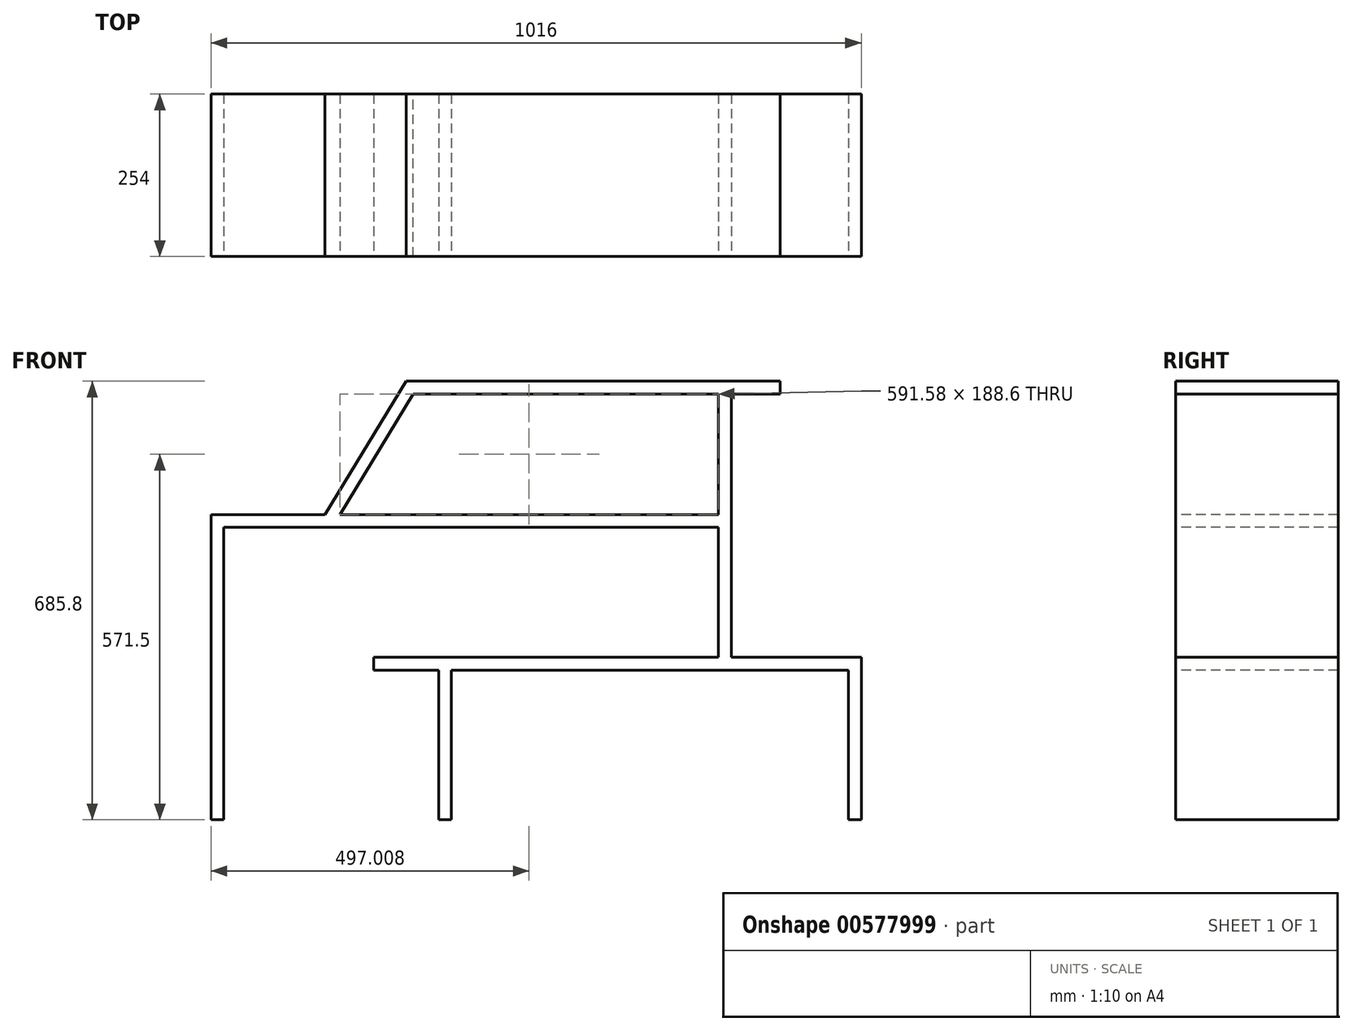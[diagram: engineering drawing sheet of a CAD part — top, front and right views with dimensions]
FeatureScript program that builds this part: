
annotation { "Feature Type Name" : "Feature", "Feature Type Description" : "" }
export const myFeature = defineFeature(function(context is Context, id is Id, definition is map)
    precondition{}
    {
        {
            var Q0;
            Q0=qCreatedBy(makeId("Top.planeOp"),FACE);
            var sketch = newSketch(context, id + "F0", { "sketchPlane" : qUnion([Q0])});
            skLineSegment(sketch, "E0", {"start": v(-526.18, 0) * mm, "end": v(427.5, 0) * mm, "construction": true});
            skLineSegment(sketch, "E1", {"start": v(0, -163.77) * mm, "end": v(0, 241.83) * mm, "construction": true});
            skLineSegment(sketch, "E2.bottom", {"start": v(488, 127) * mm, "end": v(508, 127) * mm});
            skLineSegment(sketch, "E2.top", {"start": v(488, -127) * mm, "end": v(508, -127) * mm});
            skLineSegment(sketch, "E2.left", {"start": v(488, 127) * mm, "end": v(488, -127) * mm});
            skLineSegment(sketch, "E2.right", {"start": v(508, 127) * mm, "end": v(508, -127) * mm});
            skSolve(sketch);
        }
        {
            var Q0;
            Q0=makeQuery(id+"F0.imprint","IMPRINT",FACE,{"disambiguationData":[TD([[makeQuery(id+"F0.imprint","IMPRINT",EDGE,{"derivedFrom":sQuery(id+"F0.wireOp",EDGE,"E2.bottom")}),-1.0]])]});
            extrude(context, id + "F1", {"entities" : qUnion([Q0]), "depth" : 254 * mm, "offsetDistance" : 25.4 * mm});
        }
        {
            var Q0;
            Q0=makeQuery(id+"F1.opExtrude","SWEPT_FACE",FACE,{"disambiguationData":[OSD([sQuery(id+"F0.wireOp",EDGE,"E2.top")])]});
            var sketch = newSketch(context, id + "F2", { "sketchPlane" : qUnion([Q0])});
            skLineSegment(sketch, "E3.bottom", {"start": v(508, 234) * mm, "end": v(-254, 234) * mm});
            skLineSegment(sketch, "E3.top", {"start": v(508, 254) * mm, "end": v(-254, 254) * mm});
            skLineSegment(sketch, "E3.left", {"start": v(508, 234) * mm, "end": v(508, 254) * mm});
            skLineSegment(sketch, "E3.right", {"start": v(-254, 234) * mm, "end": v(-254, 254) * mm});
            skSolve(sketch);
        }
        {
            var Q0;
            Q0=makeQuery(id+"F2.imprint","IMPRINT",FACE,{"disambiguationData":[TD([[makeQuery(id+"F2.imprint","IMPRINT",EDGE,{"derivedFrom":sQuery(id+"F2.wireOp",EDGE,"E3.top")}),1.0]])]});
            var Q1;
            Q1=makeQuery(id+"F1.opExtrude","SWEPT_FACE",FACE,{"disambiguationData":[OSD([sQuery(id+"F0.wireOp",EDGE,"E2.bottom")])]});
            extrude(context, id + "F3", {"entities" : qUnion([Q0]), "operationType" : NewBodyOperationType.ADD, "endBound" : BoundingType.UP_TO_SURFACE, "oppositeDirection" : true, "depth" : 25.4 * mm, "endBoundEntityFace" : qUnion([Q1]), "offsetDistance" : 25.4 * mm});
        }
        {
            var Q0;
            Q0=makeQuery(id+"F3.boolean.opBoolean","MERGE",FACE,{"derivedFrom":[makeQuery(id+"F1.opExtrude","SWEPT_FACE",FACE,{"disambiguationData":[OSD([sQuery(id+"F0.wireOp",EDGE,"E2.top")])]}),makeQuery(id+"F3.opExtrude","CAP_FACE",FACE,{"disambiguationData":[OSD([sQuery(id+"F2.wireOp",EDGE,"E3.bottom"),sQuery(id+"F2.wireOp",EDGE,"E3.top"),sQuery(id+"F2.wireOp",EDGE,"E3.left"),sQuery(id+"F2.wireOp",EDGE,"E3.right")])],"isStart":true})]});
            var sketch = newSketch(context, id + "F4", { "sketchPlane" : qUnion([Q0])});
            skLineSegment(sketch, "E4.bottom", {"start": v(-152.4, 234) * mm, "end": v(-132.4, 234) * mm});
            skLineSegment(sketch, "E4.top", {"start": v(-152.4, 0) * mm, "end": v(-132.4, 0) * mm});
            skLineSegment(sketch, "E4.left", {"start": v(-152.4, 234) * mm, "end": v(-152.4, 0) * mm});
            skLineSegment(sketch, "E4.right", {"start": v(-132.4, 234) * mm, "end": v(-132.4, 0) * mm});
            skSolve(sketch);
        }
        {
            var Q0;
            Q0=makeQuery(id+"F4.imprint","IMPRINT",FACE,{"disambiguationData":[TD([[makeQuery(id+"F4.imprint","IMPRINT",EDGE,{"derivedFrom":sQuery(id+"F4.wireOp",EDGE,"E4.bottom")}),1.0]])]});
            var Q1;
            {var subQ0=sQuery(id+"F0.wireOp",EDGE,"E2.bottom");Q1=makeQuery(id+"F3.boolean.opBoolean","MERGE",FACE,{"derivedFrom":[makeQuery(id+"F1.opExtrude","SWEPT_FACE",FACE,{"disambiguationData":[OSD([subQ0])]}),makeQuery(id+"F3.opExtrude","CAP_FACE",FACE,{"disambiguationData":[OSD([subQ0])],"isStart":false})]});}
            extrude(context, id + "F5", {"entities" : qUnion([Q0]), "operationType" : NewBodyOperationType.ADD, "endBound" : BoundingType.UP_TO_SURFACE, "oppositeDirection" : true, "depth" : 25.4 * mm, "endBoundEntityFace" : qUnion([Q1]), "offsetDistance" : 25.4 * mm});
        }
        {
            var Q0;
            Q0=makeQuery(id+"F5.boolean.opBoolean","MERGE",FACE,{"derivedFrom":[makeQuery(id+"F3.boolean.opBoolean","MERGE",FACE,{"derivedFrom":[makeQuery(id+"F1.opExtrude","SWEPT_FACE",FACE,{"disambiguationData":[OSD([sQuery(id+"F0.wireOp",EDGE,"E2.top")])]}),makeQuery(id+"F3.opExtrude","CAP_FACE",FACE,{"disambiguationData":[OSD([sQuery(id+"F2.wireOp",EDGE,"E3.bottom"),sQuery(id+"F2.wireOp",EDGE,"E3.top"),sQuery(id+"F2.wireOp",EDGE,"E3.left"),sQuery(id+"F2.wireOp",EDGE,"E3.right")])],"isStart":true})]}),makeQuery(id+"F5.opExtrude","CAP_FACE",FACE,{"disambiguationData":[OSD([sQuery(id+"F4.wireOp",EDGE,"E4.bottom"),sQuery(id+"F4.wireOp",EDGE,"E4.top"),sQuery(id+"F4.wireOp",EDGE,"E4.left"),sQuery(id+"F4.wireOp",EDGE,"E4.right")])],"isStart":true})]});
            var sketch = newSketch(context, id + "F6", { "sketchPlane" : qUnion([Q0])});
            skLineSegment(sketch, "E5.bottom", {"start": v(304.8, 254) * mm, "end": v(284.8, 254) * mm});
            skLineSegment(sketch, "E5.top", {"start": v(304.8, 665.8) * mm, "end": v(284.8, 665.8) * mm});
            skLineSegment(sketch, "E5.left", {"start": v(284.8, 254) * mm, "end": v(284.8, 665.8) * mm});
            skLineSegment(sketch, "E5.right", {"start": v(304.8, 254) * mm, "end": v(304.8, 665.8) * mm});
            skSolve(sketch);
        }
        {
            var Q0;
            Q0=makeQuery(id+"F6.imprint","IMPRINT",FACE,{"disambiguationData":[TD([[makeQuery(id+"F6.imprint","IMPRINT",EDGE,{"derivedFrom":sQuery(id+"F6.wireOp",EDGE,"E5.bottom")}),-1.0]])]});
            var Q1;
            Q1=makeQuery(id+"F6.imprint","IMPRINT",FACE,{"disambiguationData":[TD([[makeQuery(id+"F6.imprint","IMPRINT",EDGE,{"derivedFrom":sQuery(id+"F6.wireOp",EDGE,"E5.bottom")}),1.0]])]});
            var Q2;
            {var subQ0=sQuery(id+"F0.wireOp",EDGE,"E2.bottom");Q2=makeQuery(id+"F5.boolean.opBoolean","MERGE",FACE,{"derivedFrom":[makeQuery(id+"F3.boolean.opBoolean","MERGE",FACE,{"derivedFrom":[makeQuery(id+"F1.opExtrude","SWEPT_FACE",FACE,{"disambiguationData":[OSD([subQ0])]}),makeQuery(id+"F3.opExtrude","CAP_FACE",FACE,{"disambiguationData":[OSD([subQ0])],"isStart":false})]}),makeQuery(id+"F5.opExtrude","CAP_FACE",FACE,{"disambiguationData":[OSD([subQ0])],"isStart":false})]});}
            extrude(context, id + "F7", {"entities" : qUnion([Q0, Q1]), "operationType" : NewBodyOperationType.ADD, "endBound" : BoundingType.UP_TO_SURFACE, "oppositeDirection" : true, "depth" : 25.4 * mm, "endBoundEntityFace" : qUnion([Q2]), "offsetDistance" : 25.4 * mm});
        }
        {
            var Q0;
            Q0=makeQuery(id+"F7.boolean.opBoolean","MERGE",FACE,{"derivedFrom":[makeQuery(id+"F5.boolean.opBoolean","MERGE",FACE,{"derivedFrom":[makeQuery(id+"F3.boolean.opBoolean","MERGE",FACE,{"derivedFrom":[makeQuery(id+"F1.opExtrude","SWEPT_FACE",FACE,{"disambiguationData":[OSD([sQuery(id+"F0.wireOp",EDGE,"E2.top")])]}),makeQuery(id+"F3.opExtrude","CAP_FACE",FACE,{"disambiguationData":[OSD([sQuery(id+"F2.wireOp",EDGE,"E3.bottom"),sQuery(id+"F2.wireOp",EDGE,"E3.top"),sQuery(id+"F2.wireOp",EDGE,"E3.left"),sQuery(id+"F2.wireOp",EDGE,"E3.right")])],"isStart":true})]}),makeQuery(id+"F5.opExtrude","CAP_FACE",FACE,{"disambiguationData":[OSD([sQuery(id+"F4.wireOp",EDGE,"E4.bottom"),sQuery(id+"F4.wireOp",EDGE,"E4.top"),sQuery(id+"F4.wireOp",EDGE,"E4.left"),sQuery(id+"F4.wireOp",EDGE,"E4.right")])],"isStart":true})]}),makeQuery(id+"F7.opExtrude","CAP_FACE",FACE,{"disambiguationData":[OSD([sQuery(id+"F6.wireOp",EDGE,"E5.bottom"),sQuery(id+"F6.wireOp",EDGE,"E5.top"),sQuery(id+"F6.wireOp",EDGE,"E5.left"),sQuery(id+"F6.wireOp",EDGE,"E5.right")])],"isStart":true})]});
            var sketch = newSketch(context, id + "F8", { "sketchPlane" : qUnion([Q0])});
            skLineSegment(sketch, "E6.bottom", {"start": v(284.8, 477.2) * mm, "end": v(-508, 477.2) * mm});
            skLineSegment(sketch, "E6.top", {"start": v(284.8, 457.2) * mm, "end": v(-508, 457.2) * mm});
            skLineSegment(sketch, "E6.left", {"start": v(284.8, 477.2) * mm, "end": v(284.8, 457.2) * mm});
            skLineSegment(sketch, "E6.right", {"start": v(-508, 477.2) * mm, "end": v(-508, 457.2) * mm});
            skSolve(sketch);
        }
        {
            var Q0;
            Q0=makeQuery(id+"F8.imprint","IMPRINT",FACE,{"disambiguationData":[TD([[makeQuery(id+"F8.imprint","IMPRINT",EDGE,{"derivedFrom":sQuery(id+"F8.wireOp",EDGE,"E6.bottom")}),1.0]])]});
            var Q1;
            {var subQ0=sQuery(id+"F0.wireOp",EDGE,"E2.bottom");Q1=makeQuery(id+"F7.boolean.opBoolean","MERGE",FACE,{"derivedFrom":[makeQuery(id+"F5.boolean.opBoolean","MERGE",FACE,{"derivedFrom":[makeQuery(id+"F3.boolean.opBoolean","MERGE",FACE,{"derivedFrom":[makeQuery(id+"F1.opExtrude","SWEPT_FACE",FACE,{"disambiguationData":[OSD([subQ0])]}),makeQuery(id+"F3.opExtrude","CAP_FACE",FACE,{"disambiguationData":[OSD([subQ0])],"isStart":false})]}),makeQuery(id+"F5.opExtrude","CAP_FACE",FACE,{"disambiguationData":[OSD([subQ0])],"isStart":false})]}),makeQuery(id+"F7.opExtrude","CAP_FACE",FACE,{"disambiguationData":[OSD([subQ0])],"isStart":false})]});}
            extrude(context, id + "F9", {"entities" : qUnion([Q0]), "operationType" : NewBodyOperationType.ADD, "endBound" : BoundingType.UP_TO_SURFACE, "oppositeDirection" : true, "depth" : 25.4 * mm, "endBoundEntityFace" : qUnion([Q1]), "offsetDistance" : 25.4 * mm});
        }
        {
            var Q0;
            Q0=makeQuery(id+"FAE3QQXWs17RaLg_1.boolean.opBoolean","MERGE",FACE,{"derivedFrom":[makeQuery(id+"F7.boolean.opBoolean","MERGE",FACE,{"derivedFrom":[makeQuery(id+"F5.boolean.opBoolean","MERGE",FACE,{"derivedFrom":[makeQuery(id+"F3.boolean.opBoolean","MERGE",FACE,{"derivedFrom":[makeQuery(id+"F1.opExtrude","SWEPT_FACE",FACE,{"disambiguationData":[OSD([sQuery(id+"F0.wireOp",EDGE,"E2.top")])]}),makeQuery(id+"F3.opExtrude","CAP_FACE",FACE,{"disambiguationData":[OSD([sQuery(id+"F2.wireOp",EDGE,"E3.bottom"),sQuery(id+"F2.wireOp",EDGE,"E3.top"),sQuery(id+"F2.wireOp",EDGE,"E3.left"),sQuery(id+"F2.wireOp",EDGE,"E3.right")])],"isStart":true})]}),makeQuery(id+"F5.opExtrude","CAP_FACE",FACE,{"disambiguationData":[OSD([sQuery(id+"F4.wireOp",EDGE,"E4.bottom"),sQuery(id+"F4.wireOp",EDGE,"E4.top"),sQuery(id+"F4.wireOp",EDGE,"E4.left"),sQuery(id+"F4.wireOp",EDGE,"E4.right")])],"isStart":true})]}),makeQuery(id+"F7.opExtrude","CAP_FACE",FACE,{"disambiguationData":[OSD([sQuery(id+"F6.wireOp",EDGE,"E5.bottom"),sQuery(id+"F6.wireOp",EDGE,"E5.top"),sQuery(id+"F6.wireOp",EDGE,"E5.left"),sQuery(id+"F6.wireOp",EDGE,"E5.right")])],"isStart":true})]}),makeQuery(id+"FAE3QQXWs17RaLg_1.opExtrude","CAP_FACE",FACE,{"disambiguationData":[OSD([sQuery(id+"F8.wireOp",EDGE,"uR3yEGrp-6eCu-huob-Tspo-hjttsWu1FWy0.bottom"),sQuery(id+"F8.wireOp",EDGE,"uR3yEGrp-6eCu-huob-Tspo-hjttsWu1FWy0.top"),sQuery(id+"F8.wireOp",EDGE,"uR3yEGrp-6eCu-huob-Tspo-hjttsWu1FWy0.left"),sQuery(id+"F8.wireOp",EDGE,"uR3yEGrp-6eCu-huob-Tspo-hjttsWu1FWy0.right")])],"isStart":true})]});
            var sketch = newSketch(context, id + "F10", { "sketchPlane" : qUnion([Q0])});
            skSolve(sketch);
        }
        {
            var Q0;
            {var subQ6=sQuery(id+"F0.wireOp",EDGE,"E2.top");Q0=makeQuery(id+"F10.imprint","IMPRINT",FACE,{"disambiguationData":[TD([[makeQuery(id+"F10.imprint","IMPRINT",EDGE,{"derivedFrom":makeQuery(id+"F1.opExtrude","CAP_EDGE",EDGE,{"disambiguationData":[OSD([subQ6])],"isStart":true})}),1.0]])]});}
            var sketch = newSketch(context, id + "F11", { "sketchPlane" : qUnion([Q0])});
            skLineSegment(sketch, "E7.bottom", {"start": v(-488, 0) * mm, "end": v(-508, 0) * mm});
            skLineSegment(sketch, "E7.top", {"start": v(-488, 457.2) * mm, "end": v(-508, 457.2) * mm});
            skLineSegment(sketch, "E7.left", {"start": v(-488, 0) * mm, "end": v(-488, 457.2) * mm});
            skLineSegment(sketch, "E7.right", {"start": v(-508, 0) * mm, "end": v(-508, 457.2) * mm});
            skSolve(sketch);
        }
        {
            var Q0;
            Q0=makeQuery(id+"F11.imprint","IMPRINT",FACE,{"disambiguationData":[TD([[makeQuery(id+"F11.imprint","IMPRINT",EDGE,{"derivedFrom":sQuery(id+"F11.wireOp",EDGE,"E7.bottom")}),-1.0]])]});
            var Q1;
            {var subQ0=sQuery(id+"F0.wireOp",EDGE,"E2.bottom");Q1=makeQuery(id+"FAE3QQXWs17RaLg_1.boolean.opBoolean","MERGE",FACE,{"derivedFrom":[makeQuery(id+"F7.boolean.opBoolean","MERGE",FACE,{"derivedFrom":[makeQuery(id+"F5.boolean.opBoolean","MERGE",FACE,{"derivedFrom":[makeQuery(id+"F3.boolean.opBoolean","MERGE",FACE,{"derivedFrom":[makeQuery(id+"F1.opExtrude","SWEPT_FACE",FACE,{"disambiguationData":[OSD([subQ0])]}),makeQuery(id+"F3.opExtrude","CAP_FACE",FACE,{"disambiguationData":[OSD([subQ0])],"isStart":false})]}),makeQuery(id+"F5.opExtrude","CAP_FACE",FACE,{"disambiguationData":[OSD([subQ0])],"isStart":false})]}),makeQuery(id+"F7.opExtrude","CAP_FACE",FACE,{"disambiguationData":[OSD([subQ0])],"isStart":false})]}),makeQuery(id+"FAE3QQXWs17RaLg_1.opExtrude","CAP_FACE",FACE,{"disambiguationData":[OSD([subQ0])],"isStart":false})]});}
            extrude(context, id + "F12", {"entities" : qUnion([Q0]), "operationType" : NewBodyOperationType.ADD, "endBound" : BoundingType.UP_TO_SURFACE, "oppositeDirection" : true, "depth" : 25.4 * mm, "endBoundEntityFace" : qUnion([Q1]), "offsetDistance" : 25.4 * mm});
        }
        {
            var Q0;
            Q0=makeQuery(id+"FF1zM3mXEk5meAQ_1.boolean.opBoolean","MERGE",FACE,{"derivedFrom":[makeQuery(id+"F9.boolean.opBoolean","MERGE",FACE,{"derivedFrom":[makeQuery(id+"F7.boolean.opBoolean","MERGE",FACE,{"derivedFrom":[makeQuery(id+"F5.boolean.opBoolean","MERGE",FACE,{"derivedFrom":[makeQuery(id+"F3.boolean.opBoolean","MERGE",FACE,{"derivedFrom":[makeQuery(id+"F1.opExtrude","SWEPT_FACE",FACE,{"disambiguationData":[OSD([sQuery(id+"F0.wireOp",EDGE,"E2.top")])]}),makeQuery(id+"F3.opExtrude","CAP_FACE",FACE,{"disambiguationData":[OSD([sQuery(id+"F2.wireOp",EDGE,"E3.bottom"),sQuery(id+"F2.wireOp",EDGE,"E3.top"),sQuery(id+"F2.wireOp",EDGE,"E3.left"),sQuery(id+"F2.wireOp",EDGE,"E3.right")])],"isStart":true})]}),makeQuery(id+"F5.opExtrude","CAP_FACE",FACE,{"disambiguationData":[OSD([sQuery(id+"F4.wireOp",EDGE,"E4.bottom"),sQuery(id+"F4.wireOp",EDGE,"E4.top"),sQuery(id+"F4.wireOp",EDGE,"E4.left"),sQuery(id+"F4.wireOp",EDGE,"E4.right")])],"isStart":true})]}),makeQuery(id+"F7.opExtrude","CAP_FACE",FACE,{"disambiguationData":[OSD([sQuery(id+"F6.wireOp",EDGE,"E5.bottom"),sQuery(id+"F6.wireOp",EDGE,"E5.top"),sQuery(id+"F6.wireOp",EDGE,"E5.left"),sQuery(id+"F6.wireOp",EDGE,"E5.right")])],"isStart":true})]}),makeQuery(id+"F9.opExtrude","CAP_FACE",FACE,{"disambiguationData":[OSD([sQuery(id+"F8.wireOp",EDGE,"E6.bottom"),sQuery(id+"F8.wireOp",EDGE,"E6.top"),sQuery(id+"F8.wireOp",EDGE,"E6.left"),sQuery(id+"F8.wireOp",EDGE,"E6.right")])],"isStart":true})]}),makeQuery(id+"FF1zM3mXEk5meAQ_1.opExtrude","CAP_FACE",FACE,{"disambiguationData":[OSD([sQuery(id+"F11.wireOp",EDGE,"DvPmaQdn-qg00-ydwu-rkQD-xd9YouRA0YS0.bottom"),sQuery(id+"F11.wireOp",EDGE,"DvPmaQdn-qg00-ydwu-rkQD-xd9YouRA0YS0.top"),sQuery(id+"F11.wireOp",EDGE,"DvPmaQdn-qg00-ydwu-rkQD-xd9YouRA0YS0.left"),sQuery(id+"F11.wireOp",EDGE,"DvPmaQdn-qg00-ydwu-rkQD-xd9YouRA0YS0.right")])],"isStart":true})]});
            var sketch = newSketch(context, id + "F13", { "sketchPlane" : qUnion([Q0])});
            skLineSegment(sketch, "E8.bottom", {"start": v(-203.2, 685.8) * mm, "end": v(381, 685.8) * mm});
            skLineSegment(sketch, "E8.top", {"start": v(-203.2, 665.8) * mm, "end": v(381, 665.8) * mm});
            skLineSegment(sketch, "E8.left", {"start": v(-203.2, 685.8) * mm, "end": v(-203.2, 665.8) * mm});
            skLineSegment(sketch, "E8.right", {"start": v(381, 685.8) * mm, "end": v(381, 665.8) * mm});
            skSolve(sketch);
        }
        {
            var Q0;
            Q0=makeQuery(id+"F13.imprint","IMPRINT",FACE,{"disambiguationData":[TD([[makeQuery(id+"F13.imprint","IMPRINT",EDGE,{"derivedFrom":sQuery(id+"F13.wireOp",EDGE,"E8.bottom")}),-1.0]])]});
            var Q1;
            {var subQ0=sQuery(id+"F0.wireOp",EDGE,"E2.bottom");Q1=makeQuery(id+"FF1zM3mXEk5meAQ_1.boolean.opBoolean","MERGE",FACE,{"derivedFrom":[makeQuery(id+"F9.boolean.opBoolean","MERGE",FACE,{"derivedFrom":[makeQuery(id+"F7.boolean.opBoolean","MERGE",FACE,{"derivedFrom":[makeQuery(id+"F5.boolean.opBoolean","MERGE",FACE,{"derivedFrom":[makeQuery(id+"F3.boolean.opBoolean","MERGE",FACE,{"derivedFrom":[makeQuery(id+"F1.opExtrude","SWEPT_FACE",FACE,{"disambiguationData":[OSD([subQ0])]}),makeQuery(id+"F3.opExtrude","CAP_FACE",FACE,{"disambiguationData":[OSD([subQ0])],"isStart":false})]}),makeQuery(id+"F5.opExtrude","CAP_FACE",FACE,{"disambiguationData":[OSD([subQ0])],"isStart":false})]}),makeQuery(id+"F7.opExtrude","CAP_FACE",FACE,{"disambiguationData":[OSD([subQ0])],"isStart":false})]}),makeQuery(id+"F9.opExtrude","CAP_FACE",FACE,{"disambiguationData":[OSD([subQ0])],"isStart":false})]}),makeQuery(id+"FF1zM3mXEk5meAQ_1.opExtrude","CAP_FACE",FACE,{"disambiguationData":[OSD([subQ0])],"isStart":false})]});}
            extrude(context, id + "F14", {"entities" : qUnion([Q0]), "operationType" : NewBodyOperationType.ADD, "endBound" : BoundingType.UP_TO_SURFACE, "oppositeDirection" : true, "depth" : 25.4 * mm, "endBoundEntityFace" : qUnion([Q1]), "offsetDistance" : 25.4 * mm});
        }
        {
            var Q0;
            {var subQ6=sQuery(id+"F0.wireOp",EDGE,"E2.top");Q0=makeQuery(id+"F10.imprint","IMPRINT",FACE,{"disambiguationData":[TD([[makeQuery(id+"F10.imprint","IMPRINT",EDGE,{"derivedFrom":makeQuery(id+"F1.opExtrude","CAP_EDGE",EDGE,{"disambiguationData":[OSD([subQ6])],"isStart":true})}),1.0]])]});}
            var sketch = newSketch(context, id + "F15", { "sketchPlane" : qUnion([Q0])});
            skLineSegment(sketch, "E9", {"start": v(-330.2, 477.2) * mm, "end": v(-203.2, 685.8) * mm});
            skLineSegment(sketch, "E10", {"start": v(-203.2, 685.8) * mm, "end": v(-179.78, 685.8) * mm});
            skLineSegment(sketch, "E11", {"start": v(-179.78, 685.8) * mm, "end": v(-306.78, 477.2) * mm});
            skLineSegment(sketch, "E12", {"start": v(-306.78, 477.2) * mm, "end": v(-330.2, 477.2) * mm});
            skSolve(sketch);
        }
        {
            var Q0;
            Q0=makeQuery(id+"F15.imprint","IMPRINT",FACE,{"disambiguationData":[TD([[makeQuery(id+"F15.imprint","IMPRINT",EDGE,{"derivedFrom":sQuery(id+"F15.wireOp",EDGE,"E9")}),-1.0]])]});
            var Q1;
            {var subQ0=sQuery(id+"F0.wireOp",EDGE,"E2.bottom");Q1=makeQuery(id+"F14.boolean.opBoolean","MERGE",FACE,{"derivedFrom":[makeQuery(id+"FF1zM3mXEk5meAQ_1.boolean.opBoolean","MERGE",FACE,{"derivedFrom":[makeQuery(id+"F9.boolean.opBoolean","MERGE",FACE,{"derivedFrom":[makeQuery(id+"F7.boolean.opBoolean","MERGE",FACE,{"derivedFrom":[makeQuery(id+"F5.boolean.opBoolean","MERGE",FACE,{"derivedFrom":[makeQuery(id+"F3.boolean.opBoolean","MERGE",FACE,{"derivedFrom":[makeQuery(id+"F1.opExtrude","SWEPT_FACE",FACE,{"disambiguationData":[OSD([subQ0])]}),makeQuery(id+"F3.opExtrude","CAP_FACE",FACE,{"disambiguationData":[OSD([subQ0])],"isStart":false})]}),makeQuery(id+"F5.opExtrude","CAP_FACE",FACE,{"disambiguationData":[OSD([subQ0])],"isStart":false})]}),makeQuery(id+"F7.opExtrude","CAP_FACE",FACE,{"disambiguationData":[OSD([subQ0])],"isStart":false})]}),makeQuery(id+"F9.opExtrude","CAP_FACE",FACE,{"disambiguationData":[OSD([subQ0])],"isStart":false})]}),makeQuery(id+"FF1zM3mXEk5meAQ_1.opExtrude","CAP_FACE",FACE,{"disambiguationData":[OSD([subQ0])],"isStart":false})]}),makeQuery(id+"F14.opExtrude","CAP_FACE",FACE,{"disambiguationData":[OSD([subQ0])],"isStart":false})]});}
            extrude(context, id + "F16", {"entities" : qUnion([Q0]), "operationType" : NewBodyOperationType.ADD, "endBound" : BoundingType.UP_TO_SURFACE, "oppositeDirection" : true, "depth" : 25.4 * mm, "endBoundEntityFace" : qUnion([Q1]), "offsetDistance" : 25.4 * mm});
        }
    });
